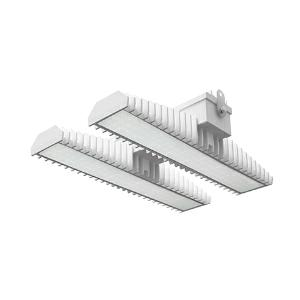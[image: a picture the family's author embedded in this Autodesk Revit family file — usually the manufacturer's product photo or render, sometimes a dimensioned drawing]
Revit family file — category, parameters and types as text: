
# Revit family: 3f_filippi_-_3f_lem_concentrato_3f_filippi_-_58888_a0812_-_3f_lem_2_led_100_cr_conc___vs_8a92
name_source: partatom
category: Lighting Fixtures
units: mm (PartAtom-declared; Revit-internal decimal feet)

## family parameters
Cut with Voids When Loaded = No
Host = Face
Light Source = No
Part Type = Normal
Room Calculation Point = No
Round Connector Dimension = Use Diameter
Shared = No

## types (1)
- 3F Filippi - 3F LEM Concentrato (1 x LED, 13214 lm, 109 W, 4000 K)
    Apparent Load = 109 VA
    Approval mark = CE
    CIE Flux Codes = 78 93 98 100 100
    Color Rendering = 80
    Color Temperature = 4000 K
    Control Gear = Electronic ballast
    Default Elevation = 1800 mm
    Description = Industrial luminaire with high light output and high luminous efficiency designed with the most innovative technologies for environments with temperature up to 55°C.

ILLUMINOTECHNICAL
Luminous efficiency 100% (DLOR 98%, ULOR 2%).
Initial luminous flux of the luminaire 13214 lm.
Direct symmetric narrow distribution: the illuminated area has a elliptical shape.
Installation Interdistance Transv.D = 0.60 x hu - Long.D = 0.91 x hu.
Tabular UGR (CIE 117 - 4H-8H; S=0.25H; 70/50/20): RUG 19.5 - 21.
Beam angle: 38° - 61°.
Luminous efficacy 121 lm/W.
Lifetime (L93/B10): 30000 h. (tq+25°C)
Lifetime (L90/B10): 50000 h. (tq+25°C)
Lifetime (L85/B10): 80000 h. (tq+25°C)
Lifetime (L80/B10): 100000 h. (tq+25°C)
Lifetime (L85/B10): 50000 h. (tq+55°C)
Sudden decreased luminous flux after 50000 hours: 0% (C0).
Photobiological safety in compliance with IEC/TR 62778: RG0 risk exempt, (IEC 62471).
In compliance with IEC/EN 62722-2-1 - IEC/EN 62717 standards.

SOURCE
2 Mid-Power linear LED modules 50W/840.
Energy efficiency class (UE 2019/2020 - UE 2019/2015): C.
CIE 13.3 Colour rendering index: CRI >80 (R9 <50%).
IES TM-30 Fidelity Index: Rf = 84 Rg = 95.
CCT nominal colour temperature 4000 K.
Colour initial tolerance (MacAdam): SDCM 3.

MECHANICAL
Passive modular heatsinks in die-casted aluminium, painted in white colour.
To optimize the thermal management of the LED module, the heatsinks are oversized and provided with self-cleaning of cooling fins.
Wiring body in aluminium and galvanised steel anchored solidly to the sinks and thermally separated.
3F Lens lenses with high luminous efficiency, transparent methacrylate (PMMA), fixed to the LED modules.
Fixing brackets in stainless steel.
Luminaire with limited surface temperature. - D - (EN 60598-2-24)
Dimensions: 470x542 mm, height 133 mm. Weight 10.06 kg.
IP65 protection degree.
Mechanical strength to impacts IK06 (1 joule).
Glow-wire test resistance 650°C.

ELECTRICAL
Halogen Free electronic wiring 230V-50/60Hz, power factor 0.97, THD <25%, constant output current, class I, 1 driver.
Power of the luminaire 109 W.
ENEC - CE.
SAFE FLICKER: PstLM=<1 and SVM=<0.4 (IEC TR 61547-1 and IEC TR 63158), to ensure a more comfortable and safe light.
Luminaire compliant with EN 60598-2-22 for power supply from a centralised emergency system CPSS (Central Power Supply System), not incorporated in the luminaire - high risk areas excluded. The default power and flux are 100% in AC and 100% in DC.
Ambient temperature from -30°C to +55°C.
Temperature class T6 max 85°C.
Quick connection via M20 3P connector with 9-13 mm tightening range.
Power unit positioned on a separate compartment by the LED module to ensure optimum temperatures of cabling components, to be inspectable and maintainable.
Relative humidity UR: <85%.

INSTALLATION
Ceiling / Suspended / Wall.
All accessories dedicated to this product are available on the Catalog and on our website www.3F-Filippi.com.

ACCESSORIES
A0812 - Anti-glare microprismatic VS moulded glass, tempered, not flammable, with sealing gasket.
One required for each light module. The pack contains 10 pieces.

APPLICATIONS
In commercial environments, exhibition and industrial areas, stores, open areas.
Applications with high ambient temperature up to 55°C.
Environments in which it is necessary a total protection against falling fragments (eg environments with foodstuffs or machines with moving parts or with extreme temperature changes), use luminaires with polycarbonate lenses.

WARNING
Fixture not suitable for cold stores with an ambient temperature <0°C and/or relative humidity >85%.
Luminaire designed for disposal/recycling at end-of-life.
Replaceable (LED only) light source by a professional. Replaceable control gear by a professional.
    Height = 133 mm  [stored 0.436352 ft]
    Lamp = 1 x LED
    Lamp Light Flux = 13214 lm
    Lamp Power = 109 W
    Lamp count = 1
    Length = 470 mm
    Lifetime = 50000 h
    Luminous efficacy = 121 lm/W
    Manufacturer = 3F Filippi
    ModVariant = No
    Model = 3F Filippi - 58888+A0812 - 3F LEM 2 LED 100 CR CONC + VS
    Mounting Place = Ceiling
    Mounting Type = Pendant
    Number of Poles = 1
    OnlyDefault = Yes
    Power Factor = 1
    Product Name = 3F Filippi - 3F LEM Concentrato
    Product group = pendant luminaire
    ProductGroupID = 9
    Protection Class = Protection class I
    Protection Degree = IP 65
    RLX_Detail_Level = 1
    RLX_Emergency_Light_Flux = 0 lm
    RLX_Emergency_Type = 0
    RLX_Emergency_Type_DB = No
    RlxData = <blob elided: 95821 chars, md5=b572b2cb>
    Socket = socket
    Standby Power = 0 W
    System Light Flux = 13214 lm
    System Power = 109 W
    Type Comments = Product without accessories
    Type Image = 3f_filippi_-_lem_2__a0812.jpg
    URL = http://relux.com
    VarID = ---
    Voltage = 0 V
    Weight = 0.00 kg
    Width = 542 mm

note: [stored X ft] marks values corroborated as IEEE doubles in the binary element streams (Revit-internal decimal feet)

## geometry (parser evidence)
native form markers: Blend x4, Sweep x12
no freeform markers — native parametric forms only
